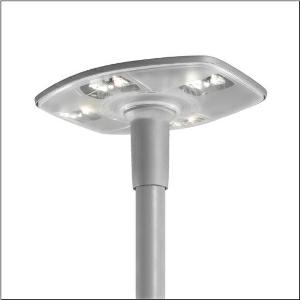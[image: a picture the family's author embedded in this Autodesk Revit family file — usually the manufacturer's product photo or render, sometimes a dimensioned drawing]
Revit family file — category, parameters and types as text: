
# Revit family: dl_r__30_led___st1_2c_5xa513271b08a5_992b
name_source: partatom
category: Lighting Fixtures
units: mm (PartAtom-declared; Revit-internal decimal feet)

## family parameters
Cut with Voids When Loaded = No
Host = Face
Light Source = No
Part Type = Normal
Room Calculation Point = No
Round Connector Dimension = Use Diameter
Shared = No

## types (1)
- --- (1 x LED, 5540 lm, 48.9 W, 4000K)
    Apparent Load = 49 VA
    CIE Flux Codes = 32 71 98 100 100
    Color Rendering = 70
    Color Temperature = 4000K
    Default Elevation = 1800 mm
    Description = DL® 30 LED, mast luminaire, primary light control with 3 zone facetted reflector, of plastic, aluminium vaporised, highly specular, primary optical cover: cover, of PMMA, structured, transparent, light distribution: ST1.2c, light emission: direct distribution, primary light characteristic: asymmetric, crossroads, installation type: post-top, LED, High Power LED, rated luminous flux: 5.540lm, luminous efficacy: 113lm/W, light colour: 740, colour temperature: 4000K, control gear: ECG Plus, control: flexible luminous flux parameterisation, time-dependent luminous flux control, constant luminous flux control, digital communication interface, power reduction, electronic power reduction, mains connection: 230..240V, AC, 50/60Hz, start of lifetime: 49W, end of service life: 51W, reduction: 23W, luminaire housing, of diecast aluminium, powder-coated, Siteco® metallic grey (DB 702S), length: 600mm, width: 510mm, height: 290mm, spigot size: d x l = 76 x 100mm (post-top) | with reducer (optional accessory) 60 x 100mm, protection rating (complete): IP66, insulation class (complete): insulation class II (safety insulation), certification: CE, ENEC, VDE, impact resistance: IK08, permissible operating ambient temperature: -25..+30°C, standard-compliant lighting for roads and squares, packaging unit: 1 piece

Light Distribution: ST1.2c
    Height = 290 mm
    Lamp = 1 x LED
    Lamp Light Flux = 5540 lm
    Lamp Power = 48.9 W
    Lamp count = 1
    Length = 510 mm
    Luminous efficacy = 113 lm/W
    Manufacturer = Siteco
    ModVariant = No
    Model = 5XA513271B08A5
    Number of Poles = 1
    OnlyDefault = Yes
    Power Factor = 1
    Product Name = DL® 30 LED | ST1.2c
    Product group = mast luminaire | pylon top
    ProductGroupID = 6100
    Protection Class = Protection class II
    Protection Degree = IP 66
    RLX_Detail_Level = 1
    RLX_Emergency_Light_Flux = 0 lm
    RLX_Emergency_Type = 0
    RLX_Emergency_Type_DB = No
    RlxData = <blob elided: 86525 chars, md5=9f48920d>
    Socket = socket
    Standby Power = 0 W
    System Light Flux = 5540 lm
    System Power = 49 W
    Type Comments = factory setting: luminous flux: 100 % | dim-lin: 254 | 497 mA
    Type Image = l_1006003.jpg
    URL = http://relux.com
    VarID = @adj_154583
    Voltage = 0 V
    Weight = 0.00 kg
    Width = 600 mm

## geometry (parser evidence)
native form markers: Blend x4, Sweep x11
no freeform markers — native parametric forms only
